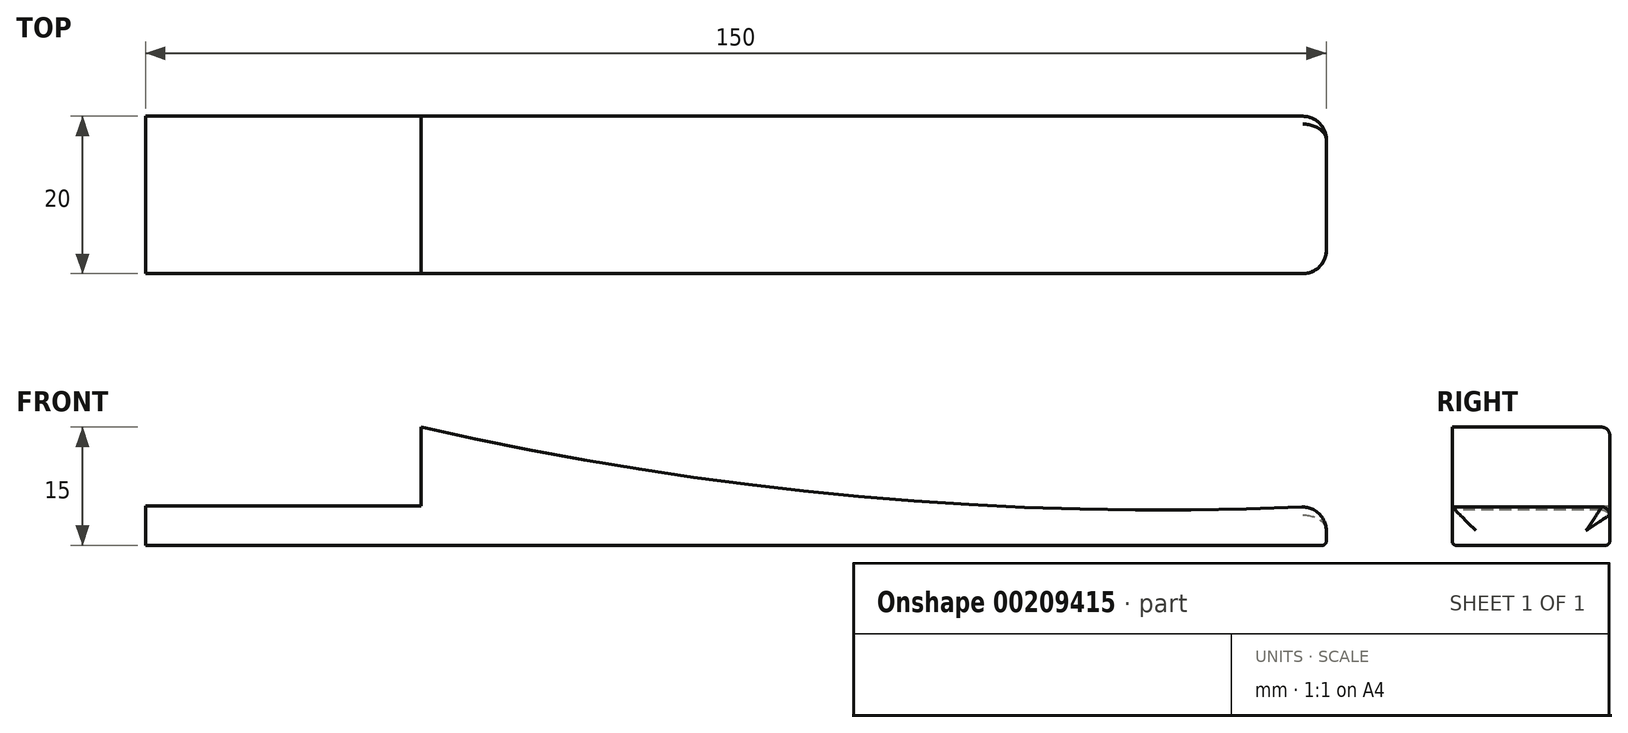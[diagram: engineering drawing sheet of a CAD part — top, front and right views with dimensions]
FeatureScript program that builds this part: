
annotation { "Feature Type Name" : "Feature", "Feature Type Description" : "" }
export const myFeature = defineFeature(function(context is Context, id is Id, definition is map)
    precondition{}
    {
        {
            var Q0;
            Q0=qCreatedBy(makeId("Top.planeOp"),FACE);
            var sketch = newSketch(context, id + "F0", { "sketchPlane" : qUnion([Q0])});
            skLineSegment(sketch, "E0.bottom", {"start": v(-75, -10) * mm, "end": v(75, -10) * mm});
            skLineSegment(sketch, "E0.top", {"start": v(-75, 10) * mm, "end": v(75, 10) * mm});
            skLineSegment(sketch, "E0.left", {"start": v(-75, -10) * mm, "end": v(-75, 10) * mm});
            skLineSegment(sketch, "E0.right", {"start": v(75, -10) * mm, "end": v(75, 10) * mm});
            skPoint(sketch, "E0.middle", {"position": v(0, 0) * mm});
            skLineSegment(sketch, "E1.bottom", {"start": v(-75, 10) * mm, "end": v(-40, 10) * mm});
            skLineSegment(sketch, "E1.top", {"start": v(-75, -10) * mm, "end": v(-40, -10) * mm});
            skLineSegment(sketch, "E1.left", {"start": v(-75, 10) * mm, "end": v(-75, -10) * mm});
            skLineSegment(sketch, "E1.right", {"start": v(-40, 10) * mm, "end": v(-40, -10) * mm});
            skSolve(sketch);
        }
        {
            var Q0;
            Q0=makeQuery(id+"F0.imprint","IMPRINT",FACE,{"disambiguationData":[TD([[makeQuery(id+"F0.imprint","IMPRINT",EDGE,{"derivedFrom":sQuery(id+"F0.wireOp",EDGE,"E0.bottom")}),1.0]])]});
            var Q1;
            Q1=makeQuery(id+"F0.imprint","IMPRINT",FACE,{"disambiguationData":[TD([[makeQuery(id+"F0.imprint","IMPRINT",EDGE,{"derivedFrom":sQuery(id+"F0.wireOp",EDGE,"E1.bottom")}),-1.0]])]});
            extrude(context, id + "F1", {"entities" : qUnion([Q0, Q1]), "depth" : 15 * mm});
        }
        {
            var Q0;
            Q0=makeQuery(id+"F1.opExtrude","CAP_FACE",FACE,{"disambiguationData":[OSD([sQuery(id+"F0.wireOp",EDGE,"E0.bottom"),sQuery(id+"F0.wireOp",EDGE,"E0.top"),sQuery(id+"F0.wireOp",EDGE,"E0.right"),sQuery(id+"F0.wireOp",EDGE,"E1.bottom"),sQuery(id+"F0.wireOp",EDGE,"E1.top"),sQuery(id+"F0.wireOp",EDGE,"E1.left")])],"isStart":false});
            var sketch = newSketch(context, id + "F2", { "sketchPlane" : qUnion([Q0])});
            skLineSegment(sketch, "E2.0", {"start": v(-40, 10) * mm, "end": v(-40, -10) * mm});
            skSolve(sketch);
        }
        {
            var Q0;
            {var subQ0=sQuery(id+"F2.wireOp",EDGE,"E2.0");Q0=makeQuery(id+"F2.imprint","IMPRINT",FACE,{"disambiguationData":[TD([[makeQuery(id+"F2.imprint","IMPRINT",EDGE,{"derivedFrom":subQ0}),-1.0]])]});}
            extrude(context, id + "F3", {"entities" : qUnion([Q0]), "operationType" : NewBodyOperationType.REMOVE, "oppositeDirection" : true, "depth" : 10 * mm});
        }
        {
            var Q0;
            Q0=makeQuery(id+"F1.opExtrude","SWEPT_FACE",FACE,{"disambiguationData":[OSD([sQuery(id+"F0.wireOp",EDGE,"E0.bottom"),sQuery(id+"F0.wireOp",EDGE,"E1.top")])]});
            var sketch = newSketch(context, id + "F4", { "sketchPlane" : qUnion([Q0])});
            skArc(sketch, "E3", {"start": v(-40, 15) * mm, "mid": v(17.16, 6.07) * mm, "end": v(75, 5) * mm});
            skSolve(sketch);
        }
        {
            var Q0;
            {var subQ0=sQuery(id+"F4.wireOp",EDGE,"E3");Q0=makeQuery(id+"F4.imprint","IMPRINT",FACE,{"disambiguationData":[TD([[makeQuery(id+"F4.imprint","IMPRINT",EDGE,{"derivedFrom":subQ0}),1.0]])]});}
            extrude(context, id + "F5", {"entities" : qUnion([Q0]), "operationType" : NewBodyOperationType.REMOVE, "endBound" : BoundingType.THROUGH_ALL, "oppositeDirection" : true, "depth" : 25 * mm});
        }
        {
            var Q0;
            Q0=makeQuery(id+"F3.boolean.opBoolean","COPY",EDGE,{"derivedFrom":makeQuery(id+"F3.opExtrude","CAP_EDGE",EDGE,{"disambiguationData":[OSD([sQuery(id+"F0.wireOp",EDGE,"E0.bottom"),sQuery(id+"F0.wireOp",EDGE,"E1.top")])],"isStart":false})});
            var Q1;
            Q1=makeQuery(id+"F3.boolean.opBoolean","COPY",EDGE,{"derivedFrom":makeQuery(id+"F3.opExtrude","SWEPT_EDGE",EDGE,{"disambiguationData":[OSD([sQuery(id+"F0.wireOp",EDGE,"E0.bottom"),sQuery(id+"F0.wireOp",EDGE,"E1.top"),sQuery(id+"F2.wireOp",EDGE,"E2.0")])]})});
            var Q2;
            Q2=makeQuery(id+"F5.boolean.opBoolean","COPY",EDGE,{"derivedFrom":makeQuery(id+"F5.opExtrude","CAP_EDGE",EDGE,{"disambiguationData":[OSD([sQuery(id+"F4.wireOp",EDGE,"E3")])],"isStart":true})});
            var Q3;
            Q3=makeQuery(id+"F5.boolean.opBoolean","COPY",EDGE,{"derivedFrom":makeQuery(id+"F5.opExtrude","SWEPT_EDGE",EDGE,{"disambiguationData":[OSD([sQuery(id+"F0.wireOp",EDGE,"E0.bottom"),sQuery(id+"F0.wireOp",EDGE,"E0.right"),sQuery(id+"F4.wireOp",EDGE,"E3")])]})});
            var Q4;
            Q4=makeQuery(id+"F5.boolean.opBoolean","INTERSECT",EDGE,{"derivedFrom":[makeQuery(id+"F1.opExtrude","SWEPT_FACE",FACE,{"disambiguationData":[OSD([sQuery(id+"F0.wireOp",EDGE,"E0.top"),sQuery(id+"F0.wireOp",EDGE,"E1.bottom")])]}),makeQuery(id+"F5.opExtrude","SWEPT_FACE",FACE,{"disambiguationData":[OSD([sQuery(id+"F4.wireOp",EDGE,"E3")])]})]});
            var Q5;
            {var subQ0=sQuery(id+"F2.wireOp",EDGE,"E2.0");Q5=makeQuery(id+"F5.boolean.opBoolean","MERGE",EDGE,{"derivedFrom":[makeQuery(id+"F3.boolean.opBoolean","COPY",EDGE,{"derivedFrom":makeQuery(id+"F3.opExtrude","CAP_EDGE",EDGE,{"disambiguationData":[OSD([subQ0])],"isStart":true})}),makeQuery(id+"F5.opExtrude","SWEPT_EDGE",EDGE,{"disambiguationData":[OSD([sQuery(id+"F0.wireOp",EDGE,"E0.bottom"),sQuery(id+"F0.wireOp",EDGE,"E1.top"),subQ0,sQuery(id+"F4.wireOp",EDGE,"E3")])]})]});}
            var Q6;
            Q6=makeQuery(id+"F3.boolean.opBoolean","COPY",EDGE,{"derivedFrom":makeQuery(id+"F3.opExtrude","SWEPT_EDGE",EDGE,{"disambiguationData":[OSD([sQuery(id+"F0.wireOp",EDGE,"E0.top"),sQuery(id+"F0.wireOp",EDGE,"E1.bottom"),sQuery(id+"F2.wireOp",EDGE,"E2.0")])]})});
            var Q7;
            Q7=makeQuery(id+"F3.boolean.opBoolean","COPY",EDGE,{"derivedFrom":makeQuery(id+"F3.opExtrude","CAP_EDGE",EDGE,{"disambiguationData":[OSD([sQuery(id+"F0.wireOp",EDGE,"E0.top"),sQuery(id+"F0.wireOp",EDGE,"E1.bottom")])],"isStart":false})});
            var Q8;
            Q8=makeQuery(id+"F3.boolean.opBoolean","COPY",EDGE,{"derivedFrom":makeQuery(id+"F3.opExtrude","CAP_EDGE",EDGE,{"disambiguationData":[OSD([sQuery(id+"F0.wireOp",EDGE,"E1.left")])],"isStart":false})});
            fillet(context, id + "F6", {"entities" : qUnion([Q0, Q1, Q2, Q3, Q4, Q5, Q6, Q7, Q8]), "radius" : 1 * mm, "tangentPropagation" : true, "allowEdgeOverflow" : false});
        }
        {
            var Q0;
            Q0=makeQuery(id+"F1.opExtrude","CAP_EDGE",EDGE,{"disambiguationData":[OSD([sQuery(id+"F0.wireOp",EDGE,"E0.top"),sQuery(id+"F0.wireOp",EDGE,"E1.bottom")])],"isStart":true});
            var Q1;
            Q1=makeQuery(id+"F1.opExtrude","CAP_EDGE",EDGE,{"disambiguationData":[OSD([sQuery(id+"F0.wireOp",EDGE,"E1.left")])],"isStart":true});
            var Q2;
            Q2=makeQuery(id+"F1.opExtrude","CAP_EDGE",EDGE,{"disambiguationData":[OSD([sQuery(id+"F0.wireOp",EDGE,"E0.bottom"),sQuery(id+"F0.wireOp",EDGE,"E1.top")])],"isStart":true});
            var Q3;
            Q3=makeQuery(id+"F1.opExtrude","CAP_EDGE",EDGE,{"disambiguationData":[OSD([sQuery(id+"F0.wireOp",EDGE,"E0.right")])],"isStart":true});
            fillet(context, id + "F7", {"entities" : qUnion([Q0, Q1, Q2, Q3]), "radius" : .5 * mm, "tangentPropagation" : true, "allowEdgeOverflow" : false});
        }
        {
            var Q0;
            Q0=makeQuery(id+"F1.opExtrude","SWEPT_EDGE",EDGE,{"disambiguationData":[OSD([sQuery(id+"F0.wireOp",EDGE,"E0.top"),sQuery(id+"F0.wireOp",EDGE,"E0.right")])]});
            var Q1;
            Q1=makeQuery(id+"F1.opExtrude","SWEPT_EDGE",EDGE,{"disambiguationData":[OSD([sQuery(id+"F0.wireOp",EDGE,"E0.bottom"),sQuery(id+"F0.wireOp",EDGE,"E0.right")])]});
            var Q2;
            Q2=makeQuery(id+"F1.opExtrude","SWEPT_EDGE",EDGE,{"disambiguationData":[OSD([sQuery(id+"F0.wireOp",EDGE,"E1.top"),sQuery(id+"F0.wireOp",EDGE,"E1.left")])]});
            var Q3;
            Q3=makeQuery(id+"F1.opExtrude","SWEPT_EDGE",EDGE,{"disambiguationData":[OSD([sQuery(id+"F0.wireOp",EDGE,"E1.bottom"),sQuery(id+"F0.wireOp",EDGE,"E1.left")])]});
            fillet(context, id + "F8", {"entities" : qUnion([Q0, Q1, Q2, Q3]), "radius" : 3 * mm, "tangentPropagation" : true, "allowEdgeOverflow" : false});
        }
    });
